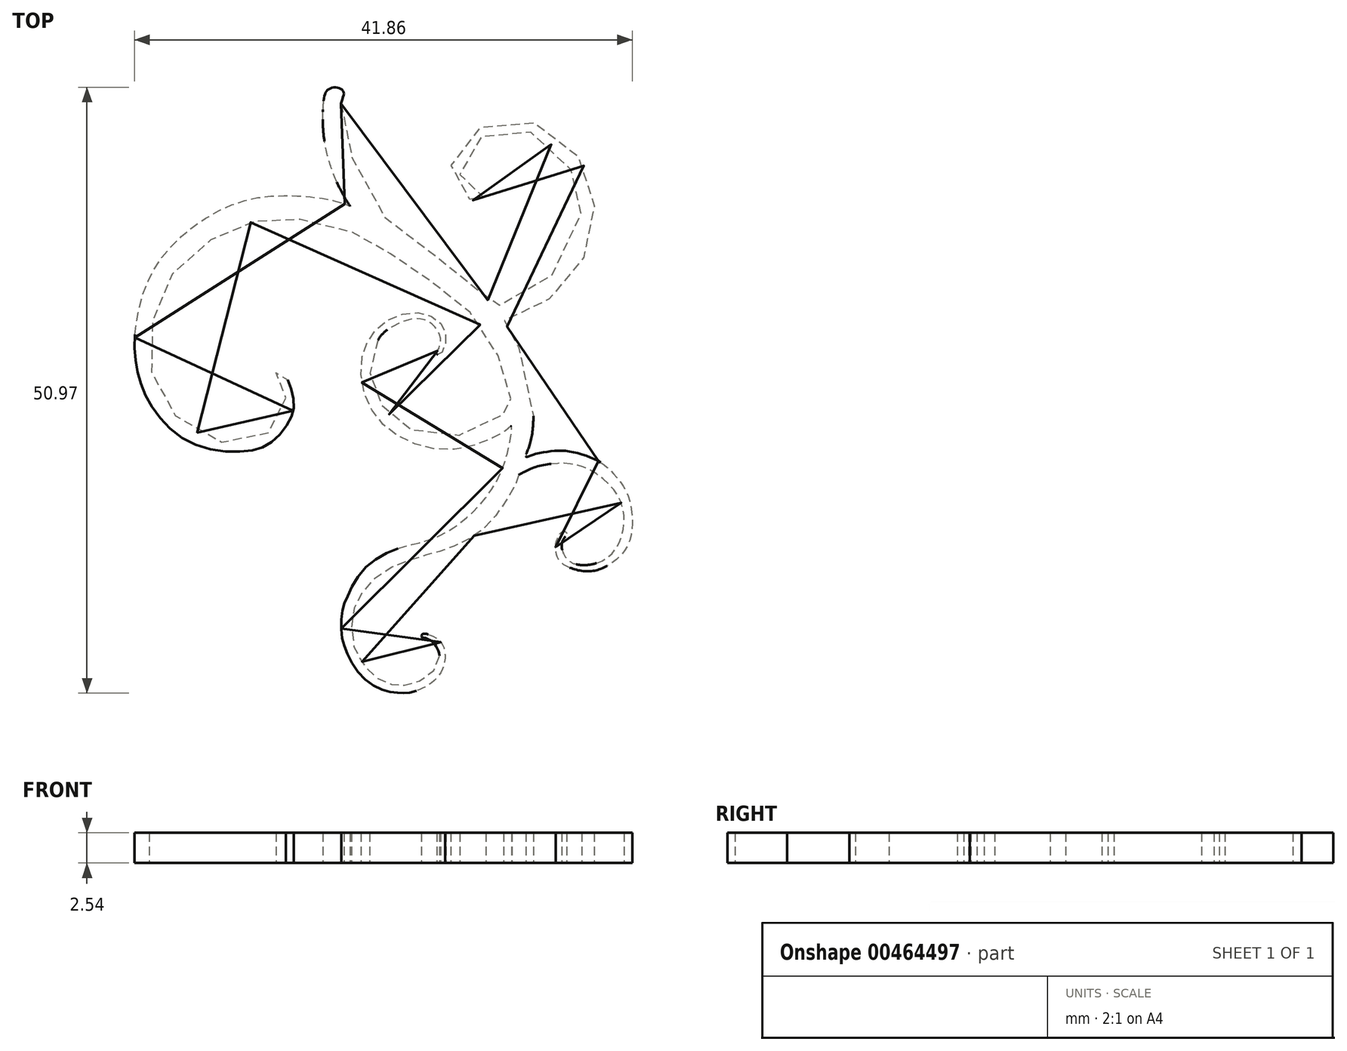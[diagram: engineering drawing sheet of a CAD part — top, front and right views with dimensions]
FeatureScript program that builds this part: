
annotation { "Feature Type Name" : "Feature", "Feature Type Description" : "" }
export const myFeature = defineFeature(function(context is Context, id is Id, definition is map)
    precondition{}
    {
        {
            var Q0;
            Q0=qCreatedBy(makeId("Top.planeOp"),FACE);
            var sketch = newSketch(context, id + "F0", { "sketchPlane" : qUnion([Q0])});
            skPoint(sketch, "E0.middle", {"position": v(0, 0) * mm});
            skPoint(sketch, "E1.115.internal.snap0", {"position": v(8.8, -24.97) * mm});
            skFitSpline(sketch, "E1", {"points": [v(3.99, 24.61) * mm, v(4.37, 22.32) * mm, v(5.51, 18.32) * mm, v(8.18, 14.5) * mm, v(11.24, 12.2) * mm, v(14.48, 10.11) * mm, v(16, 8.4) * mm, v(16.6, 7.75) * mm, v(16.66, 7.55) * mm, v(16.86, 7.55) * mm, v(18.89, 8.16) * mm, v(22.33, 10.92) * mm, v(24.15, 15.17) * mm, v(24.15, 16.6) * mm, v(23.32, 19.07) * mm, v(21.57, 21.25) * mm, v(18.6, 22.56) * mm, v(16.32, 22.13) * mm, v(14.4, 20.55) * mm, v(13.96, 18.9) * mm, v(14.4, 17.47) * mm, v(15.54, 16.8) * mm, v(16.01, 16.75) * mm, v(16.17, 16.64) * mm, v(16.12, 16.49) * mm, v(15.86, 16.38) * mm, v(15.02, 16.49) * mm, v(14.14, 17) * mm, v(13.26, 18.62) * mm, v(13.72, 20.7) * mm, v(15.39, 22.42) * mm, v(18.2, 23.3) * mm, v(21.06, 22.68) * mm, v(23.5, 20.75) * mm, v(24.9, 18.2) * mm, v(25.27, 15.6) * mm, v(24.65, 12.32) * mm, v(24.13, 11.18) * mm, v(22.18, 8.73) * mm, v(19, 6.8) * mm, v(17.76, 6.37) * mm, v(17.66, 6.3) * mm, v(17.73, 6.18) * mm, v(17.93, 5.89) * mm, v(18.94, 4.05) * mm, v(20.12, -0.66) * mm, v(19.82, -4.19) * mm, v(19.53, -5.07) * mm, v(19.62, -5.12) * mm, v(19.93, -5) * mm, v(21.48, -4.66) * mm, v(23.24, -4.66) * mm, v(25.5, -5.4) * mm, v(26.61, -6.23) * mm, v(27.9, -7.9) * mm, v(28.47, -10.19) * mm, v(28, -12.73) * mm, v(26.13, -14.4) * mm, v(24.31, -14.71) * mm, v(22.6, -14.09) * mm, v(22.13, -13.36) * mm, v(22.07, -12.32) * mm, v(22.5, -11.49) * mm, v(22.75, -11.38) * mm, v(22.96, -11.49) * mm, v(22.85, -11.8) * mm, v(22.65, -12.11) * mm, v(22.54, -12.73) * mm, v(23.01, -13.72) * mm, v(24, -14.2) * mm, v(25.5, -14.04) * mm, v(27.07, -12.9) * mm, v(27.8, -10.4) * mm, v(27.02, -8) * mm, v(24.52, -6.02) * mm, v(22.28, -5.66) * mm, v(20.15, -6.02) * mm, v(19.06, -6.54) * mm, v(18.95, -6.6) * mm, v(18.9, -6.8) * mm, v(18.43, -7.84) * mm, v(16.77, -10.34) * mm, v(15.1, -11.8) * mm, v(13.23, -12.73) * mm, v(11.77, -13.2) * mm, v(10.24, -13.64) * mm, v(7.54, -14.79) * mm, v(5.65, -16.68) * mm, v(4.9, -18.77) * mm, v(5.18, -21.4) * mm, v(5.72, -22.28) * mm, v(6.42, -23.25) * mm, v(7.94, -24.17) * mm, v(9.18, -24.33) * mm, v(10.87, -23.81) * mm, v(12.23, -22.25) * mm, v(11.83, -20.84) * mm, v(11.1, -20.36) * mm, v(10.79, -20.28) * mm, v(10.75, -20.16) * mm, v(10.87, -20) * mm, v(11.4, -20.08) * mm, v(12.4, -20.72) * mm, v(12.71, -22.2) * mm, v(12.03, -23.73) * mm, v(10.67, -24.65) * mm, v(9.59, -24.97) * mm, v(8.8, -24.97) * mm, v(7.46, -24.7) * mm, v(5.7, -23.53) * mm, v(4.45, -21.52) * mm, v(4.05, -20.12) * mm, v(4.09, -18.12) * mm, v(4.5, -16.91) * mm, v(5.92, -14.56) * mm, v(8.8, -12.8) * mm, v(11.6, -12.02) * mm, v(14.5, -10.27) * mm, v(17.38, -6.5) * mm, v(18.34, -2.75) * mm, v(18.3, -2.51) * mm, v(18.17, -2.63) * mm, v(17.5, -3.11) * mm, v(14.4, -4.36) * mm, v(10.63, -4.16) * mm, v(7.7, -2.55) * mm, v(6.02, 0) * mm, v(5.72, 3.16) * mm, v(6.64, 5.25) * mm, v(8.25, 6.57) * mm, v(10.54, 7.01) * mm, v(12.06, 6.4) * mm, v(12.7, 5.53) * mm, v(12.78, 4.52) * mm, v(12.5, 3.72) * mm, v(12.26, 3.48) * mm, v(12.06, 3.52) * mm, v(12.06, 3.72) * mm, v(12.18, 3.96) * mm, v(12.34, 4.89) * mm, v(11.42, 6.2) * mm, v(10.01, 6.5) * mm, v(8.6, 6) * mm, v(7.45, 5.2) * mm, v(6.72, 3.84) * mm, v(6.4, 2) * mm, v(6.76, 0.43) * mm, v(8, -1.53) * mm, v(9.76, -2.77) * mm, v(13.17, -3.38) * mm, v(17.1, -1.98) * mm, v(18.16, -1.02) * mm, v(18.32, -0.9) * mm, v(18.35, -0.77) * mm, v(18, 1) * mm, v(16.7, 4.4) * mm, v(14.2, 7.67) * mm, v(11.08, 9.96) * mm, v(8.11, 12) * mm, v(5.67, 13.45) * mm, v(1.66, 14.75) * mm, v(-2.34, 14.8) * mm, v(-4.6, 14.33) * mm, v(-8.57, 12.06) * mm, v(-10.83, 9.22) * mm, v(-12.08, 5.14) * mm, v(-11.74, 1.28) * mm, v(-9.59, -2.01) * mm, v(-5.62, -3.94) * mm, v(-2.21, -3.15) * mm, v(-0.74, -0.88) * mm, v(-0.85, 0.71) * mm, v(-1.4, 1.8) * mm, v(-1.47, 2.04) * mm, v(-1.28, 2.16) * mm, v(-1.04, 2.04) * mm, v(-0.54, 1.45) * mm, v(0, -0.4) * mm, v(-0.3, -1.94) * mm, v(-1.81, -3.83) * mm, v(-4, -4.63) * mm, v(-8.25, -4.1) * mm, v(-11.61, -1.37) * mm, v(-13.02, 1.6) * mm, v(-13.38, 4.56) * mm, v(-12.52, 9.04) * mm, v(-9.9, 13) * mm, v(-5.26, 16.07) * mm, v(-0.94, 16.87) * mm, v(3.03, 16.53) * mm, v(4.5, 16.07) * mm, v(4.72, 15.96) * mm, v(4.72, 16.02) * mm, v(4.44, 16.45) * mm, v(3.34, 18.72) * mm, v(2.55, 21.7) * mm, v(2.46, 24.05) * mm, v(2.64, 25.41) * mm, v(2.9, 25.8) * mm, v(3.51, 25.98) * mm, v(4.04, 25.8) * mm, v(4.21, 25.41) * mm, v(3.99, 24.61) * mm]});
            skSolve(sketch);
        }
        {
            var Q0;
            Q0 = qSketchRegion(id + "F0", true);
            extrude(context, id + "F1", {"entities" : qUnion([Q0]), "depth" : 2.54 * mm});
        }
    });
